# Revit family: Plum Fix_Shower_Argent_Pallas OH Shower + 250 arm
name_source: partatom
category: Plumbing Fixtures
revit_build: Autodesk Revit 2016 (Build: 20150220_1215(x64)
units: mm (PartAtom-declared; Revit-internal decimal feet)

## family parameters
Always vertical = Yes
Cut with Voids When Loaded = No
OmniClass Number = 23.45.05.14.17
OmniClass Title = Showers
Part Type = Normal
Room Calculation Point = No
Round Connector Dimension = Use Diameter
Shared = No
Work Plane-Based = No

## types (1)
- Chrome (OH212301)
    Body Material = z_Argent_Chrome
    CW Connection = No
    Cost = 0 $
    Description = Pallas 230 Overhead Shower on 250 Wall Arm
    HW Connection = Yes
    IfcExportAs = IfcSanitaryTerminal
    IfcExportType = SHOWER
    Manufacturer = Argent
    Manufacturer_Overall Depth = 365 mm
    Manufacturer_Overall Height = 177.5 mm
    Manufacturer_Overall Width = 230 mm
    Manufacturer_Spec Code = OH212301
    Manufacturer_URL__Product Specific = https://www.argentaust.com.au
    Model = OH212301
    ModifiedIssue_ANZRS = 20200402 $
    Type Comments = Chrome Finish
    URL = https://www.argentaust.com.au
    Uniclass2015Code = Pr_40_20_87_75
    Uniclass2015Title = Shower fittings package
    Uniclass2015Version = Products v1.17
    Vent Connection = No
    Waste Connection = No

## geometry (parser evidence)
native form markers: Sweep x3
no freeform markers — native parametric forms only
